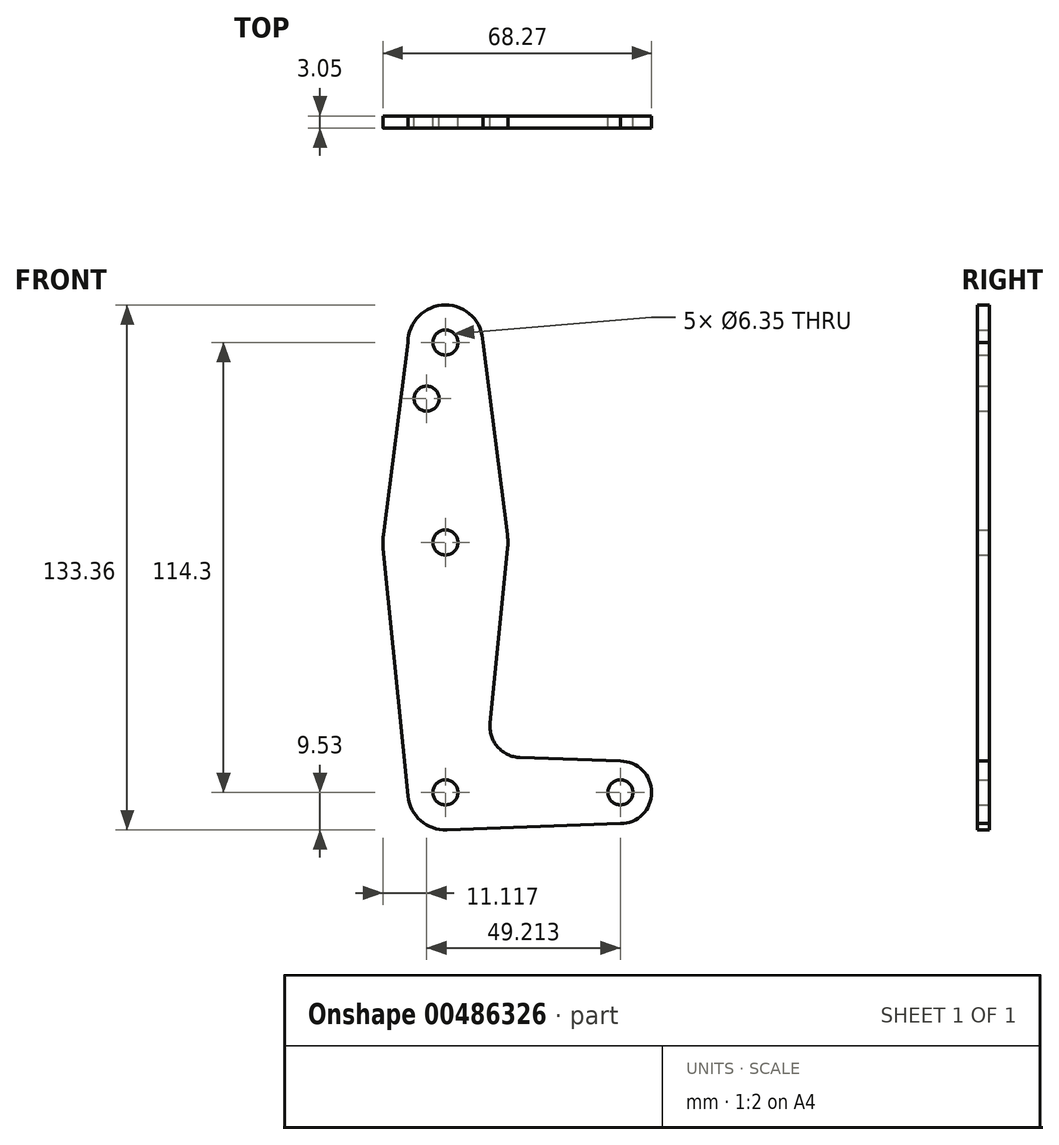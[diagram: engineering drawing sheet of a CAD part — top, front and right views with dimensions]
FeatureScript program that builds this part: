
annotation { "Feature Type Name" : "Feature", "Feature Type Description" : "" }
export const myFeature = defineFeature(function(context is Context, id is Id, definition is map)
    precondition{}
    {
        {
            var Q0;
            Q0=qCreatedBy(makeId("Front.planeOp"),FACE);
            var sketch = newSketch(context, id + "F0", { "sketchPlane" : qUnion([Q0])});
            skLineSegment(sketch, "E0", {"start": v(0, 0) * mm, "end": v(0, 114.3) * mm, "construction": true});
            skLineSegment(sketch, "E1", {"start": v(0, 0) * mm, "end": v(44.45, 0) * mm, "construction": true});
            skCircle(sketch, "E2", {"center": v(0, 0) * mm, "radius": 9.53 * mm});
            skCircle(sketch, "E3", {"center": v(44.45, 0) * mm, "radius": 7.94 * mm});
            skCircle(sketch, "E4", {"center": v(0, 63.5) * mm, "radius": 15.88 * mm});
            skCircle(sketch, "E5", {"center": v(0, 114.3) * mm, "radius": 9.53 * mm});
            skLineSegment(sketch, "E6", {"start": v(0.34, -9.52) * mm, "end": v(44.45, -7.94) * mm});
            skCircle(sketch, "E7", {"center": v(0, 114.3) * mm, "radius": 3.18 * mm});
            skCircle(sketch, "E8", {"center": v(0, 63.5) * mm, "radius": 3.18 * mm});
            skCircle(sketch, "E9", {"center": v(0, 0) * mm, "radius": 3.18 * mm});
            skCircle(sketch, "E10", {"center": v(44.45, 0) * mm, "radius": 3.18 * mm});
            skLineSegment(sketch, "E11", {"start": v(-9.52, 114.3) * mm, "end": v(-15.75, 65.5) * mm});
            skLineSegment(sketch, "E12", {"start": v(9.52, 114.3) * mm, "end": v(15.75, 65.5) * mm});
            skCircle(sketch, "E13", {"center": v(-4.76, 100.03) * mm, "radius": 3.18 * mm});
            skLineSegment(sketch, "E14", {"start": v(15.8, 61.91) * mm, "end": v(11.34, 17.6) * mm});
            skLineSegment(sketch, "E15", {"start": v(44.45, 7.94) * mm, "end": v(18.97, 8.85) * mm});
            skLineSegment(sketch, "E16", {"start": v(-9.48, -0.95) * mm, "end": v(-15.8, 61.91) * mm});
            skPoint(sketch, "E17.newPointB", {"position": v(0, 9.53) * mm});
            skArc(sketch, "E17.filletArc", {"start": v(11.34, 17.6) * mm, "mid": v(13.26, 11.57) * mm, "end": v(18.97, 8.85) * mm});
            skSolve(sketch);
        }
        {
            var Q0;
            Q0 = qSketchRegion(id + "F0", true);
            extrude(context, id + "F1", {"entities" : qUnion([Q0]), "depth" : 3.05 * mm});
        }
    });
